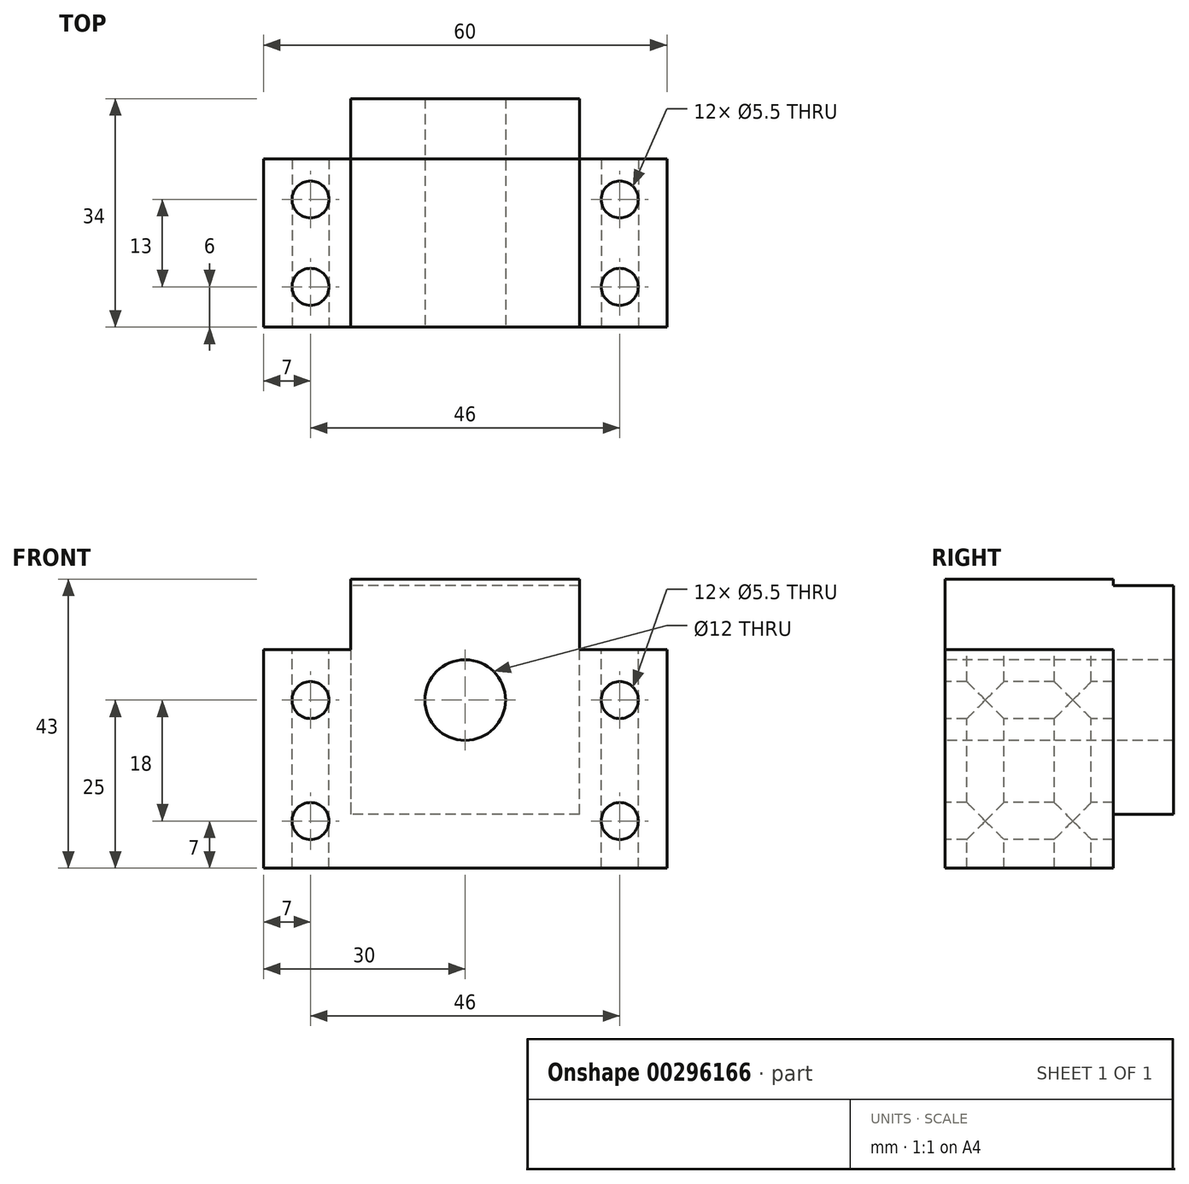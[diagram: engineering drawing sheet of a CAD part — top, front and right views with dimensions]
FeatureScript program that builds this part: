
annotation { "Feature Type Name" : "Feature", "Feature Type Description" : "" }
export const myFeature = defineFeature(function(context is Context, id is Id, definition is map)
    precondition{}
    {
        {
            var Q0;
            Q0=qCreatedBy(makeId("Front.planeOp"),FACE);
            var sketch = newSketch(context, id + "F0", { "sketchPlane" : qUnion([Q0])});
            skLineSegment(sketch, "E0.bottom", {"start": v(17, 21.5) * mm, "end": v(-17, 21.5) * mm});
            skLineSegment(sketch, "E0.top", {"start": v(30, -21.5) * mm, "end": v(-30, -21.5) * mm});
            skLineSegment(sketch, "E0.left", {"start": v(30, 11) * mm, "end": v(30, -21.5) * mm});
            skLineSegment(sketch, "E0.right", {"start": v(-30, 11) * mm, "end": v(-30, -21.5) * mm});
            skPoint(sketch, "E0.middle", {"position": v(0, 0) * mm});
            skLineSegment(sketch, "E1", {"start": v(0, -21.5) * mm, "end": v(0, 3.5) * mm, "construction": true});
            skCircle(sketch, "E2", {"center": v(0, 3.5) * mm, "radius": 6 * mm});
            skLineSegment(sketch, "E3", {"start": v(30, 11) * mm, "end": v(17, 11) * mm});
            skLineSegment(sketch, "E4", {"start": v(17, 11) * mm, "end": v(17, 21.5) * mm});
            skPoint(sketch, "E5.orphan", {"position": v(30, 21.5) * mm});
            skLineSegment(sketch, "E6.MirrorCS", {"start": v(-17, 11) * mm, "end": v(-17, 21.5) * mm});
            skLineSegment(sketch, "E7.MirrorCS", {"start": v(-30, 11) * mm, "end": v(-17, 11) * mm});
            skPoint(sketch, "E8.orphan", {"position": v(-30, 21.5) * mm});
            skSolve(sketch);
        }
        {
            var Q0;
            Q0=makeQuery(id+"F0.imprint","IMPRINT",FACE,{"disambiguationData":[TD([[makeQuery(id+"F0.imprint","IMPRINT",EDGE,{"derivedFrom":sQuery(id+"F0.wireOp",EDGE,"E0.bottom")}),1.0]])]});
            extrude(context, id + "F1", {"entities" : qUnion([Q0]), "oppositeDirection" : true, "depth" : 25 * mm, "offsetDistance" : 25 * mm});
        }
        {
            var Q0;
            Q0=makeQuery(id+"F1.opExtrude","CAP_FACE",FACE,{"disambiguationData":[OSD([sQuery(id+"F0.wireOp",EDGE,"E0.bottom"),sQuery(id+"F0.wireOp",EDGE,"E0.top"),sQuery(id+"F0.wireOp",EDGE,"E0.left"),sQuery(id+"F0.wireOp",EDGE,"E0.right"),sQuery(id+"F0.wireOp",EDGE,"E2")])],"isStart":true});
            var sketch = newSketch(context, id + "F2", { "sketchPlane" : qUnion([Q0])});
            skLineSegment(sketch, "E9", {"start": v(-43.2, -21.5) * mm, "end": v(-43.2, 3.5) * mm, "construction": true});
            skLineSegment(sketch, "E10", {"start": v(-43.2, 3.5) * mm, "end": v(16.8, 3.5) * mm, "construction": true});
            skCircle(sketch, "E11", {"center": v(-23, 3.5) * mm, "radius": 2.75 * mm});
            skCircle(sketch, "E12", {"center": v(23, 3.5) * mm, "radius": 2.75 * mm});
            skLineSegment(sketch, "E13", {"start": v(0, -21.5) * mm, "end": v(0, 21.5) * mm, "construction": true});
            skLineSegment(sketch, "E14", {"start": v(-43.2, 3.5) * mm, "end": v(-43.2, -14.5) * mm, "construction": true});
            skLineSegment(sketch, "E15", {"start": v(-43.2, -14.5) * mm, "end": v(16.8, -14.5) * mm, "construction": true});
            skCircle(sketch, "E16", {"center": v(-23, -14.5) * mm, "radius": 2.75 * mm});
            skCircle(sketch, "E17", {"center": v(23, -14.5) * mm, "radius": 2.75 * mm});
            skSolve(sketch);
        }
        {
            var Q0;
            Q0=makeQuery(id+"F2.imprint","IMPRINT",FACE,{"disambiguationData":[TD([[makeQuery(id+"F2.imprint","IMPRINT",EDGE,{"derivedFrom":sQuery(id+"F2.wireOp",EDGE,"E12")}),1.0]])]});
            var Q1;
            Q1=makeQuery(id+"F2.imprint","IMPRINT",FACE,{"disambiguationData":[TD([[makeQuery(id+"F2.imprint","IMPRINT",EDGE,{"derivedFrom":sQuery(id+"F2.wireOp",EDGE,"E16")}),1.0]])]});
            var Q2;
            Q2=makeQuery(id+"F2.imprint","IMPRINT",FACE,{"disambiguationData":[TD([[makeQuery(id+"F2.imprint","IMPRINT",EDGE,{"derivedFrom":sQuery(id+"F2.wireOp",EDGE,"E17")}),1.0]])]});
            var Q3;
            Q3=makeQuery(id+"F2.imprint","IMPRINT",FACE,{"disambiguationData":[TD([[makeQuery(id+"F2.imprint","IMPRINT",EDGE,{"derivedFrom":sQuery(id+"F2.wireOp",EDGE,"E11")}),1.0]])]});
            extrude(context, id + "F3", {"entities" : qUnion([Q0, Q1, Q2, Q3]), "operationType" : NewBodyOperationType.REMOVE, "endBound" : BoundingType.THROUGH_ALL, "oppositeDirection" : true, "depth" : 25 * mm});
        }
        {
            var Q0;
            Q0=makeQuery(id+"F1.opExtrude","SWEPT_FACE",FACE,{"disambiguationData":[OSD([sQuery(id+"F0.wireOp",EDGE,"E0.bottom")])]});
            var sketch = newSketch(context, id + "F4", { "sketchPlane" : qUnion([Q0])});
            skLineSegment(sketch, "E18", {"start": v(0, 25) * mm, "end": v(-23, 25) * mm, "construction": true});
            skLineSegment(sketch, "E19", {"start": v(-23, 25) * mm, "end": v(-23, 0) * mm, "construction": true});
            skLineSegment(sketch, "E20", {"start": v(0, 25) * mm, "end": v(23, 25) * mm, "construction": true});
            skLineSegment(sketch, "E21", {"start": v(23, 25) * mm, "end": v(23, 0) * mm, "construction": true});
            skLineSegment(sketch, "E22", {"start": v(17, 0) * mm, "end": v(17, 19) * mm, "construction": true});
            skLineSegment(sketch, "E23", {"start": v(17, 19) * mm, "end": v(30, 19) * mm, "construction": true});
            skLineSegment(sketch, "E24", {"start": v(30, 19) * mm, "end": v(30, 6) * mm, "construction": true});
            skLineSegment(sketch, "E25", {"start": v(30, 6) * mm, "end": v(-23, 6) * mm, "construction": true});
            skCircle(sketch, "E26", {"center": v(-23, 6) * mm, "radius": 2.75 * mm});
            skCircle(sketch, "E27", {"center": v(-23, 19) * mm, "radius": 2.75 * mm});
            skCircle(sketch, "E28", {"center": v(23, 19) * mm, "radius": 2.75 * mm});
            skCircle(sketch, "E29", {"center": v(23, 6) * mm, "radius": 2.75 * mm});
            skSolve(sketch);
        }
        {
            var Q0;
            Q0=makeQuery(id+"F4.imprint","IMPRINT",FACE,{"disambiguationData":[TD([[makeQuery(id+"F4.imprint","IMPRINT",EDGE,{"derivedFrom":sQuery(id+"F4.wireOp",EDGE,"E27")}),1.0]])]});
            var Q1;
            Q1=makeQuery(id+"F4.imprint","IMPRINT",FACE,{"disambiguationData":[TD([[makeQuery(id+"F4.imprint","IMPRINT",EDGE,{"derivedFrom":sQuery(id+"F4.wireOp",EDGE,"E26")}),1.0]])]});
            var Q2;
            Q2=makeQuery(id+"F4.imprint","IMPRINT",FACE,{"disambiguationData":[TD([[makeQuery(id+"F4.imprint","IMPRINT",EDGE,{"derivedFrom":sQuery(id+"F4.wireOp",EDGE,"E29")}),1.0]])]});
            var Q3;
            Q3=makeQuery(id+"F4.imprint","IMPRINT",FACE,{"disambiguationData":[TD([[makeQuery(id+"F4.imprint","IMPRINT",EDGE,{"derivedFrom":sQuery(id+"F4.wireOp",EDGE,"E28")}),1.0]])]});
            extrude(context, id + "F5", {"entities" : qUnion([Q0, Q1, Q2, Q3]), "operationType" : NewBodyOperationType.REMOVE, "endBound" : BoundingType.THROUGH_ALL, "oppositeDirection" : true, "depth" : 25 * mm});
        }
        {
            var Q0;
            Q0=makeQuery(id+"F1.opExtrude","CAP_FACE",FACE,{"disambiguationData":[OSD([sQuery(id+"F0.wireOp",EDGE,"E0.bottom"),sQuery(id+"F0.wireOp",EDGE,"E0.top"),sQuery(id+"F0.wireOp",EDGE,"E0.left"),sQuery(id+"F0.wireOp",EDGE,"E0.right"),sQuery(id+"F0.wireOp",EDGE,"E2")])],"isStart":false});
            var sketch = newSketch(context, id + "F6", { "sketchPlane" : qUnion([Q0])});
            skLineSegment(sketch, "E30.bottom", {"start": v(-17, 20.5) * mm, "end": v(17, 20.5) * mm});
            skLineSegment(sketch, "E30.top", {"start": v(-17, -13.5) * mm, "end": v(17, -13.5) * mm});
            skLineSegment(sketch, "E30.left", {"start": v(-17, 20.5) * mm, "end": v(-17, -13.5) * mm});
            skLineSegment(sketch, "E30.right", {"start": v(17, 20.5) * mm, "end": v(17, -13.5) * mm});
            skPoint(sketch, "E30.middle", {"position": v(0, 3.5) * mm});
            skSolve(sketch);
        }
        {
            var Q0;
            Q0=makeQuery(id+"F6.imprint","IMPRINT",FACE,{"disambiguationData":[TD([[makeQuery(id+"F6.imprint","IMPRINT",EDGE,{"derivedFrom":sQuery(id+"F6.wireOp",EDGE,"E30.bottom")}),-1.0]])]});
            extrude(context, id + "F7", {"entities" : qUnion([Q0]), "operationType" : NewBodyOperationType.ADD, "depth" : 9 * mm, "offsetDistance" : 25 * mm});
        }
    });
